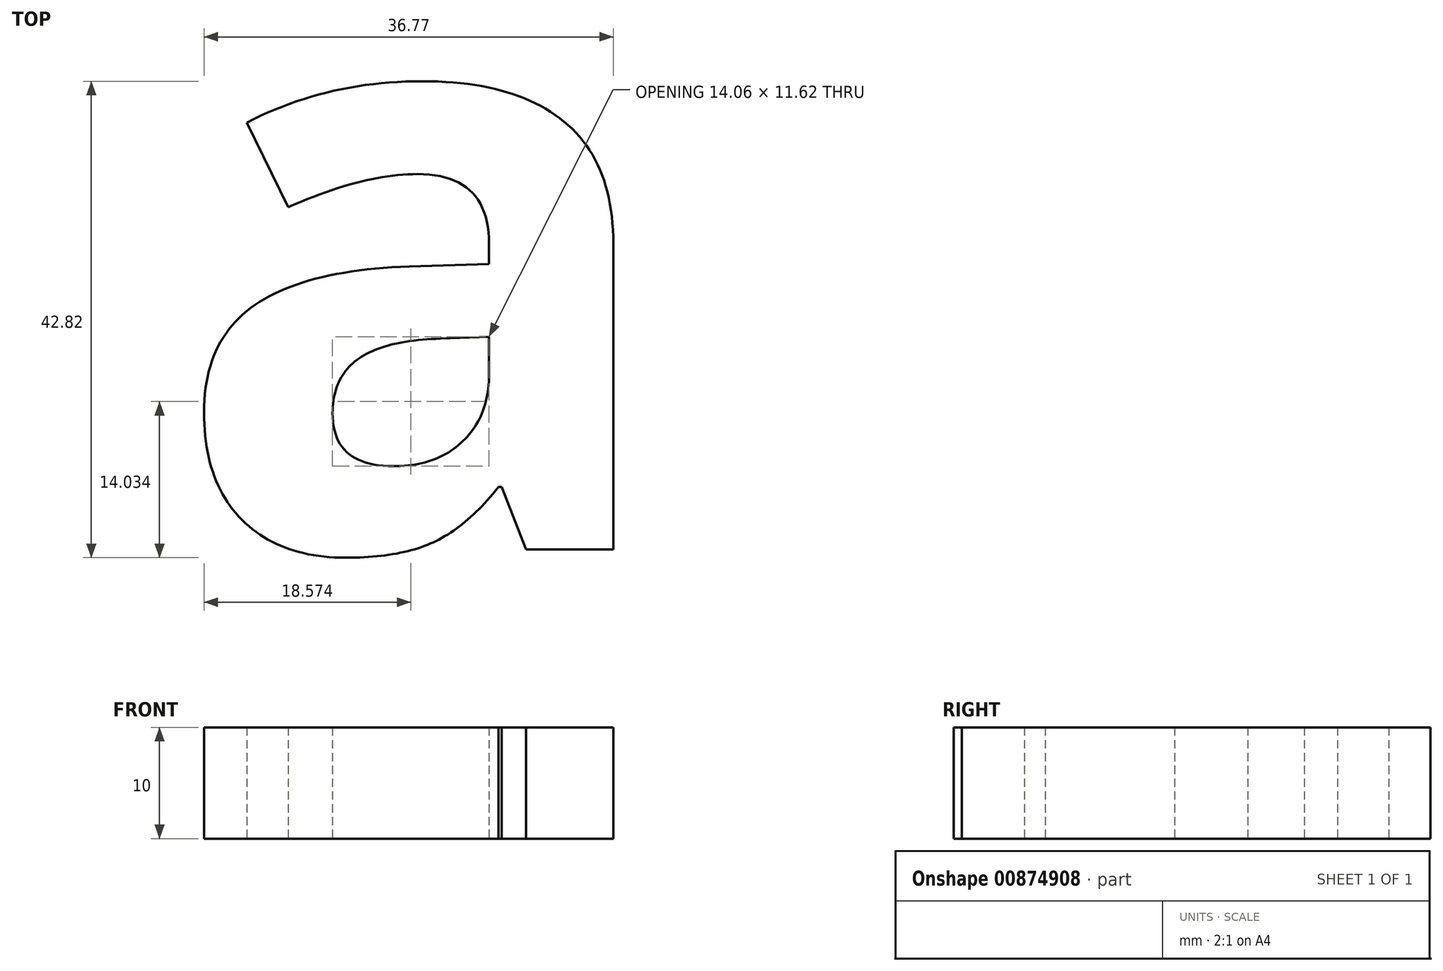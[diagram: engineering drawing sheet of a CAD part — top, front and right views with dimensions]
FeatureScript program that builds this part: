
annotation { "Feature Type Name" : "Feature", "Feature Type Description" : "" }
export const myFeature = defineFeature(function(context is Context, id is Id, definition is map)
    precondition{}
    {
        {
            var Q0;
            Q0=qCreatedBy(makeId("Top.planeOp"),FACE);
            var sketch = newSketch(context, id + "F0", { "sketchPlane" : qUnion([Q0])});
            skText(sketch, "E0", { "text": "a", "fontName": "OpenSans-Bold.ttf"});
            const initialGuessF0  = {"E0": [0, 0, 1, 0, 0.05438]};
            skSetInitialGuess(sketch, initialGuessF0);
            skSolve(sketch);
        }
        {
            var Q0;
            Q0 = qSketchRegion(id + "F0", true);
            extrude(context, id + "F1", {"entities" : qUnion([Q0]), "depth" : 10 * mm, "offsetDistance" : 25 * mm});
        }
    });
